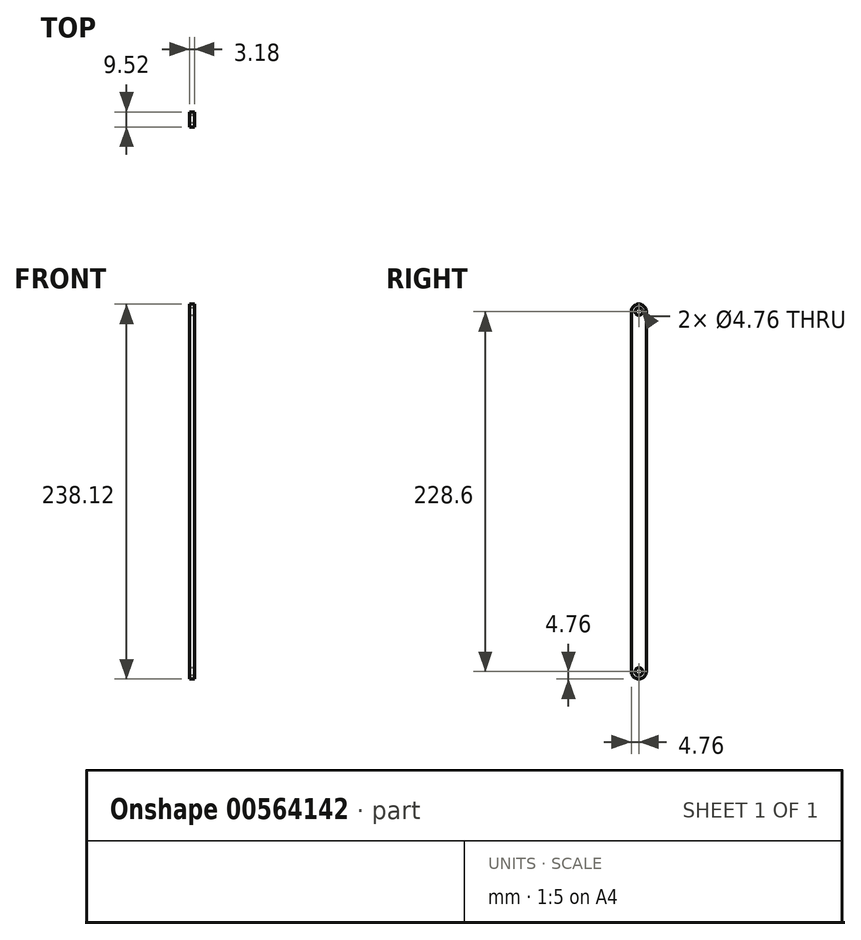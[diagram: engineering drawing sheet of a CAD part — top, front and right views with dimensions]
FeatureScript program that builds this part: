
annotation { "Feature Type Name" : "Feature", "Feature Type Description" : "" }
export const myFeature = defineFeature(function(context is Context, id is Id, definition is map)
    precondition{}
    {
        {
            var Q0;
            Q0=qCreatedBy(makeId("Right.planeOp"),FACE);
            var sketch = newSketch(context, id + "F0", { "sketchPlane" : qUnion([Q0])});
            skCircle(sketch, "E0", {"center": v(0, 0) * mm, "radius": 2.38 * mm});
            skCircle(sketch, "E1", {"center": v(0, 228.6) * mm, "radius": 2.38 * mm});
            skCircle(sketch, "E2", {"center": v(0, 228.6) * mm, "radius": 4.76 * mm});
            skCircle(sketch, "E3", {"center": v(0, 0) * mm, "radius": 4.76 * mm});
            skLineSegment(sketch, "E4", {"start": v(-4.76, 228.6) * mm, "end": v(-4.76, 0) * mm});
            skLineSegment(sketch, "E5", {"start": v(4.76, 228.6) * mm, "end": v(4.76, 0) * mm});
            skSolve(sketch);
        }
        {
            var Q0;
            Q0 = qSketchRegion(id + "F0", true);
            extrude(context, id + "F1", {"entities" : qUnion([Q0]), "depth" : 3.17 * mm, "offsetDistance" : 25.4 * mm});
        }
    });
